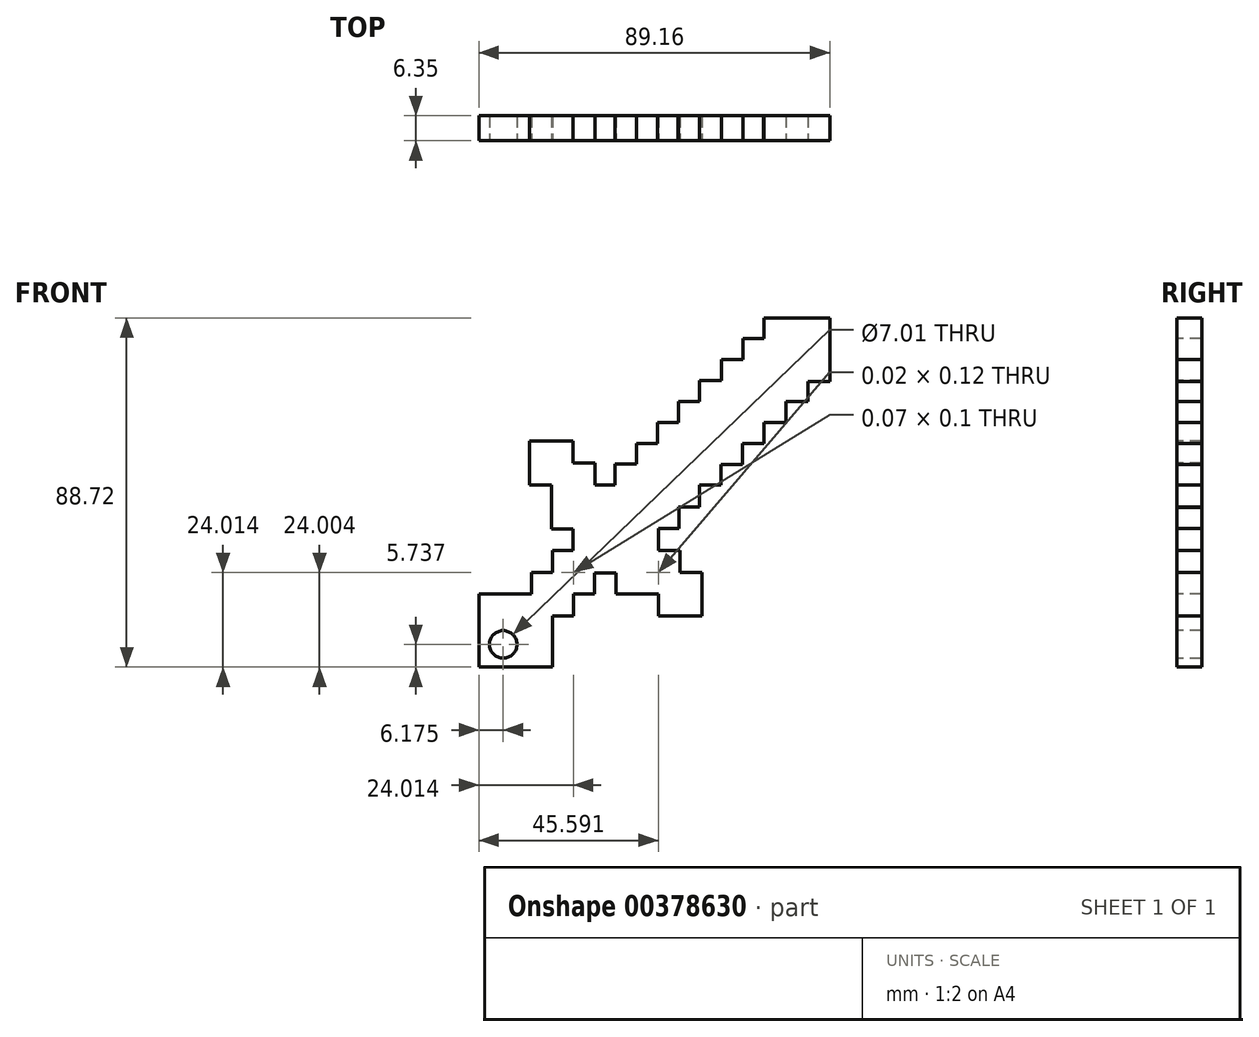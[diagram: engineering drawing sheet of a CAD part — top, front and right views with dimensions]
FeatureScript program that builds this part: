
annotation { "Feature Type Name" : "Feature", "Feature Type Description" : "" }
export const myFeature = defineFeature(function(context is Context, id is Id, definition is map)
    precondition{}
    {
        {
            var Q0;
            Q0=qCreatedBy(makeId("Front.planeOp"),FACE);
            var sketch = newSketch(context, id + "F0", { "sketchPlane" : qUnion([Q0])});
            skLineSegment(sketch, "E0.bottom", {"start": v(-54.91, -24.94) * mm, "end": v(-36.22, -24.94) * mm});
            skLineSegment(sketch, "E0.top", {"start": v(-54.91, -43.46) * mm, "end": v(-36.22, -43.46) * mm});
            skLineSegment(sketch, "E0.left", {"start": v(-54.91, -24.94) * mm, "end": v(-54.91, -43.46) * mm});
            skLineSegment(sketch, "E0.right", {"start": v(-36.22, -24.94) * mm, "end": v(-36.22, -43.46) * mm});
            skPoint(sketch, "E1", {"position": v(-45.57, -34.2) * mm});
            skPoint(sketch, "E2.orphan", {"position": v(-45.57, -24.94) * mm});
            skPoint(sketch, "E3.orphan", {"position": v(-36.22, -34.2) * mm});
            skPoint(sketch, "E4.end.orphan", {"position": v(-45.57, -43.46) * mm});
            skPoint(sketch, "E5.start.orphan", {"position": v(-54.91, -34.2) * mm});
            skLineSegment(sketch, "E6.bottom", {"start": v(-41.62, -37.8) * mm, "end": v(-49.52, -37.8) * mm});
            skLineSegment(sketch, "E6.top", {"start": v(-41.62, -30.6) * mm, "end": v(-49.52, -30.6) * mm});
            skLineSegment(sketch, "E6.left", {"start": v(-41.62, -37.8) * mm, "end": v(-41.62, -30.6) * mm});
            skLineSegment(sketch, "E6.right", {"start": v(-49.52, -37.8) * mm, "end": v(-49.52, -30.6) * mm});
            skLineSegment(sketch, "E7.bottom", {"start": v(-30.86, -19.4) * mm, "end": v(-41.59, -19.4) * mm});
            skLineSegment(sketch, "E7.top", {"start": v(-30.86, -30.48) * mm, "end": v(-41.59, -30.48) * mm});
            skLineSegment(sketch, "E7.left", {"start": v(-30.86, -19.4) * mm, "end": v(-30.86, -30.48) * mm});
            skLineSegment(sketch, "E7.right", {"start": v(-41.59, -19.4) * mm, "end": v(-41.59, -30.48) * mm});
            skPoint(sketch, "E7.middle", {"position": v(-36.22, -24.94) * mm});
            skLineSegment(sketch, "E8.bottom", {"start": v(-25.5, -24.94) * mm, "end": v(-36.22, -24.94) * mm});
            skLineSegment(sketch, "E8.top", {"start": v(-25.5, -13.87) * mm, "end": v(-36.22, -13.87) * mm});
            skLineSegment(sketch, "E8.left", {"start": v(-25.5, -24.94) * mm, "end": v(-25.5, -13.87) * mm});
            skLineSegment(sketch, "E8.right", {"start": v(-36.22, -24.94) * mm, "end": v(-36.22, -13.87) * mm});
            skPoint(sketch, "E8.middle", {"position": v(-30.86, -19.4) * mm});
            skLineSegment(sketch, "E9.bottom", {"start": v(-20.13, -8.39) * mm, "end": v(-30.93, -8.39) * mm});
            skLineSegment(sketch, "E9.left", {"start": v(-20.13, -8.39) * mm, "end": v(-20.13, -19.35) * mm});
            skPoint(sketch, "E9.middle", {"position": v(-25.5, -13.87) * mm});
            skLineSegment(sketch, "E10.bottom", {"start": v(-14.86, -13.87) * mm, "end": v(-25.5, -13.87) * mm});
            skLineSegment(sketch, "E10.top", {"start": v(-14.86, -2.91) * mm, "end": v(-20.23, -2.91) * mm});
            skLineSegment(sketch, "E10.left", {"start": v(-14.86, -8.39) * mm, "end": v(-14.86, -2.91) * mm});
            skLineSegment(sketch, "E10.right", {"start": v(-25.4, -13.87) * mm, "end": v(-25.4, -2.91) * mm});
            skPoint(sketch, "E10.middle", {"position": v(-20.13, -8.39) * mm});
            skLineSegment(sketch, "E11.bottom", {"start": v(-9.5, -8.39) * mm, "end": v(-20.23, -8.39) * mm});
            skLineSegment(sketch, "E11.right", {"start": v(-20.23, -8.39) * mm, "end": v(-20.23, 2.73) * mm});
            skPoint(sketch, "E11.middle", {"position": v(-14.86, -2.91) * mm});
            skPoint(sketch, "E11.cornerSnap0", {"position": v(-14.86, -8.39) * mm});
            skPoint(sketch, "E12.middle", {"position": v(-9.5, 2.57) * mm});
            skLineSegment(sketch, "E13.bottom", {"start": v(-4.16, -2.9) * mm, "end": v(-14.84, -2.9) * mm});
            skLineSegment(sketch, "E13.top", {"start": v(-4.16, 8.04) * mm, "end": v(-14.84, 8.04) * mm});
            skLineSegment(sketch, "E13.left", {"start": v(-4.16, -2.9) * mm, "end": v(-4.16, 8.04) * mm});
            skLineSegment(sketch, "E13.right", {"start": v(-14.84, -2.9) * mm, "end": v(-14.84, 8.04) * mm});
            skLineSegment(sketch, "E14.bottom", {"start": v(1.16, 2.73) * mm, "end": v(-9.49, 2.73) * mm});
            skLineSegment(sketch, "E14.top", {"start": v(1.16, 13.36) * mm, "end": v(-9.49, 13.36) * mm});
            skLineSegment(sketch, "E14.left", {"start": v(1.16, 2.73) * mm, "end": v(1.16, 13.36) * mm});
            skLineSegment(sketch, "E14.right", {"start": v(-9.49, 2.73) * mm, "end": v(-9.49, 13.36) * mm});
            skPoint(sketch, "E14.middle", {"position": v(-4.16, 8.04) * mm});
            skLineSegment(sketch, "E15.bottom", {"start": v(6.6, 8.04) * mm, "end": v(-4.28, 8.04) * mm});
            skLineSegment(sketch, "E15.top", {"start": v(6.6, 18.68) * mm, "end": v(-4.28, 18.68) * mm});
            skLineSegment(sketch, "E15.left", {"start": v(6.6, 8.04) * mm, "end": v(6.6, 18.68) * mm});
            skLineSegment(sketch, "E15.right", {"start": v(-4.28, 8.04) * mm, "end": v(-4.28, 18.68) * mm});
            skPoint(sketch, "E15.middle", {"position": v(1.16, 13.36) * mm});
            skPoint(sketch, "E15.cornerSnap0", {"position": v(1.16, 8.04) * mm});
            skLineSegment(sketch, "E16.bottom", {"start": v(12.14, 13.36) * mm, "end": v(1.06, 13.36) * mm});
            skLineSegment(sketch, "E16.top", {"start": v(12.14, 24) * mm, "end": v(1.06, 24) * mm});
            skLineSegment(sketch, "E16.left", {"start": v(12.14, 13.36) * mm, "end": v(12.14, 24) * mm});
            skLineSegment(sketch, "E16.right", {"start": v(1.06, 13.36) * mm, "end": v(1.06, 24) * mm});
            skPoint(sketch, "E16.middle", {"position": v(6.6, 18.68) * mm});
            skLineSegment(sketch, "E17.bottom", {"start": v(17.58, 18.68) * mm, "end": v(6.7, 18.68) * mm});
            skLineSegment(sketch, "E17.top", {"start": v(17.58, 29.3) * mm, "end": v(6.7, 29.3) * mm});
            skLineSegment(sketch, "E17.left", {"start": v(17.58, 18.68) * mm, "end": v(17.58, 29.3) * mm});
            skLineSegment(sketch, "E17.right", {"start": v(6.7, 18.68) * mm, "end": v(6.7, 29.3) * mm});
            skPoint(sketch, "E17.middle", {"position": v(12.14, 24) * mm});
            skLineSegment(sketch, "E18.bottom", {"start": v(23.03, 24) * mm, "end": v(12.14, 24) * mm});
            skLineSegment(sketch, "E18.top", {"start": v(23.03, 34.62) * mm, "end": v(12.14, 34.62) * mm});
            skLineSegment(sketch, "E18.left", {"start": v(23.03, 24) * mm, "end": v(23.03, 34.62) * mm});
            skLineSegment(sketch, "E18.right", {"start": v(12.14, 24) * mm, "end": v(12.14, 34.62) * mm});
            skPoint(sketch, "E18.middle", {"position": v(17.58, 29.3) * mm});
            skLineSegment(sketch, "E19.bottom", {"start": v(28.63, 29.3) * mm, "end": v(17.42, 29.3) * mm});
            skLineSegment(sketch, "E19.top", {"start": v(28.63, 39.94) * mm, "end": v(17.42, 39.94) * mm});
            skLineSegment(sketch, "E19.left", {"start": v(28.63, 29.3) * mm, "end": v(28.63, 39.94) * mm});
            skLineSegment(sketch, "E19.right", {"start": v(17.42, 29.3) * mm, "end": v(17.42, 39.94) * mm});
            skPoint(sketch, "E19.middle", {"position": v(23.03, 34.62) * mm});
            skLineSegment(sketch, "E20.bottom", {"start": v(28.63, 34.62) * mm, "end": v(23.04, 34.62) * mm});
            skLineSegment(sketch, "E20.top", {"start": v(34.23, 45.26) * mm, "end": v(23.04, 45.26) * mm});
            skLineSegment(sketch, "E20.left", {"start": v(34.23, 34.62) * mm, "end": v(34.23, 45.26) * mm});
            skLineSegment(sketch, "E20.right", {"start": v(23.04, 34.62) * mm, "end": v(23.04, 39.94) * mm});
            skPoint(sketch, "E20.middle", {"position": v(28.63, 39.94) * mm});
            skLineSegment(sketch, "E21.bottom", {"start": v(-30.93, 2.73) * mm, "end": v(-9.33, 2.73) * mm});
            skLineSegment(sketch, "E21.top", {"start": v(-30.93, -19.5) * mm, "end": v(-9.33, -19.5) * mm});
            skLineSegment(sketch, "E21.left", {"start": v(-30.93, 2.73) * mm, "end": v(-30.93, -19.5) * mm});
            skLineSegment(sketch, "E21.right", {"start": v(-9.33, 2.73) * mm, "end": v(-9.33, -19.5) * mm});
            skLineSegment(sketch, "E22", {"start": v(-25.4, -2.91) * mm, "end": v(-25.4, 2.73) * mm});
            skLineSegment(sketch, "E23", {"start": v(-14.86, -13.87) * mm, "end": v(-9.33, -13.87) * mm});
            skLineSegment(sketch, "E24.MirrorCS", {"start": v(-36.47, -2.91) * mm, "end": v(-36.47, 2.73) * mm});
            skLineSegment(sketch, "E25.MirrorCS", {"start": v(-30.93, 2.73) * mm, "end": v(-36.47, 2.73) * mm});
            skLineSegment(sketch, "E26.MirrorCS", {"start": v(-36.47, -8.39) * mm, "end": v(-30.93, -8.39) * mm});
            skLineSegment(sketch, "E27.MirrorCS", {"start": v(-36.47, -8.39) * mm, "end": v(-36.47, -2.91) * mm});
            skPoint(sketch, "E28.orphan", {"position": v(-36.47, -13.87) * mm});
            skPoint(sketch, "E29.orphan", {"position": v(-41.73, -8.39) * mm});
            skPoint(sketch, "E30.orphan", {"position": v(-52.54, 2.73) * mm});
            skLineSegment(sketch, "E31.top", {"start": v(-25.4, 8.37) * mm, "end": v(-36.47, 8.37) * mm});
            skLineSegment(sketch, "E31.left", {"start": v(-25.4, -2.91) * mm, "end": v(-25.4, 8.37) * mm});
            skLineSegment(sketch, "E31.right", {"start": v(-36.47, -2.91) * mm, "end": v(-36.47, 8.37) * mm});
            skPoint(sketch, "E31.middle", {"position": v(-30.93, 2.73) * mm});
            skLineSegment(sketch, "E32.bottom", {"start": v(-30.93, 2.73) * mm, "end": v(-42, 2.73) * mm});
            skLineSegment(sketch, "E32.top", {"start": v(-30.93, 14) * mm, "end": v(-42, 14) * mm});
            skLineSegment(sketch, "E32.left", {"start": v(-30.93, 2.73) * mm, "end": v(-30.93, 14) * mm});
            skLineSegment(sketch, "E32.right", {"start": v(-42, 2.73) * mm, "end": v(-42, 14) * mm});
            skPoint(sketch, "E32.middle", {"position": v(-36.47, 8.37) * mm});
            skPoint(sketch, "E33.orphan", {"position": v(-31, -8.39) * mm});
            skPoint(sketch, "E34.orphan", {"position": v(-30.86, -8.39) * mm});
            skPoint(sketch, "E35.orphan", {"position": v(-30.86, -19.35) * mm});
            skLineSegment(sketch, "E36.bottom", {"start": v(-14.84, -24.85) * mm, "end": v(-20.13, -24.85) * mm});
            skLineSegment(sketch, "E36.left", {"start": v(-14.84, -19.5) * mm, "end": v(-14.84, -13.85) * mm});
            skPoint(sketch, "E36.middle", {"position": v(-20.13, -19.35) * mm});
            skLineSegment(sketch, "E37", {"start": v(-20.13, -19.35) * mm, "end": v(-20.13, -24.85) * mm});
            skLineSegment(sketch, "E38.bottom", {"start": v(-14.84, -19.5) * mm, "end": v(-9.3, -19.5) * mm});
            skLineSegment(sketch, "E38.top", {"start": v(-14.84, -24.92) * mm, "end": v(-9.3, -24.92) * mm});
            skLineSegment(sketch, "E38.left", {"start": v(-14.84, -24.85) * mm, "end": v(-14.84, -24.92) * mm});
            skLineSegment(sketch, "E38.right", {"start": v(-9.3, -19.5) * mm, "end": v(-9.3, -24.92) * mm});
            skLineSegment(sketch, "E39.bottom", {"start": v(-9.33, -13.87) * mm, "end": v(-3.78, -13.87) * mm});
            skLineSegment(sketch, "E39.top", {"start": v(-9.33, -19.39) * mm, "end": v(-3.78, -19.39) * mm});
            skLineSegment(sketch, "E39.left", {"start": v(-9.33, -13.87) * mm, "end": v(-9.33, -19.39) * mm});
            skLineSegment(sketch, "E39.right", {"start": v(-3.78, -13.87) * mm, "end": v(-3.78, -19.39) * mm});
            skLineSegment(sketch, "E40.bottom", {"start": v(-3.78, -19.39) * mm, "end": v(-9.3, -19.39) * mm});
            skLineSegment(sketch, "E40.top", {"start": v(-3.78, -24.92) * mm, "end": v(-9.3, -24.92) * mm});
            skLineSegment(sketch, "E40.left", {"start": v(-3.78, -19.39) * mm, "end": v(-3.78, -24.92) * mm});
            skLineSegment(sketch, "E40.right", {"start": v(-9.3, -19.39) * mm, "end": v(-9.3, -24.92) * mm});
            skPoint(sketch, "E41.orphan", {"position": v(0, -13.87) * mm});
            skLineSegment(sketch, "E42.bottom", {"start": v(1.76, -30.45) * mm, "end": v(-9.3, -30.45) * mm});
            skLineSegment(sketch, "E42.top", {"start": v(1.76, -19.39) * mm, "end": v(-9.3, -19.39) * mm});
            skLineSegment(sketch, "E42.left", {"start": v(1.76, -30.45) * mm, "end": v(1.76, -19.39) * mm});
            skLineSegment(sketch, "E42.right", {"start": v(-9.3, -30.45) * mm, "end": v(-9.3, -19.39) * mm});
            skPoint(sketch, "E42.middle", {"position": v(-3.78, -24.92) * mm});
            skLineSegment(sketch, "E43.bottom", {"start": v(-9.5, 8.04) * mm, "end": v(-14.92, 8.04) * mm});
            skLineSegment(sketch, "E43.top", {"start": v(-9.49, 13.36) * mm, "end": v(-14.92, 13.36) * mm});
            skLineSegment(sketch, "E43.right", {"start": v(-14.92, 8.04) * mm, "end": v(-14.92, 13.36) * mm});
            skPoint(sketch, "E44.firstSnap0", {"position": v(-14.84, 2.57) * mm});
            skLineSegment(sketch, "E44.bottom", {"start": v(-14.84, 2.73) * mm, "end": v(-20.27, 2.73) * mm});
            skLineSegment(sketch, "E44.top", {"start": v(-14.84, 8.07) * mm, "end": v(-20.27, 8.07) * mm});
            skLineSegment(sketch, "E44.left", {"start": v(-14.84, 2.73) * mm, "end": v(-14.84, 8.07) * mm});
            skLineSegment(sketch, "E44.right", {"start": v(-20.27, 2.73) * mm, "end": v(-20.27, 8.07) * mm});
            skLineSegment(sketch, "E45.bottom", {"start": v(-4.16, 13.36) * mm, "end": v(-9.49, 13.36) * mm});
            skLineSegment(sketch, "E45.top", {"start": v(-4.16, 18.64) * mm, "end": v(-9.49, 18.64) * mm});
            skLineSegment(sketch, "E45.right", {"start": v(-9.49, 13.36) * mm, "end": v(-9.49, 18.64) * mm});
            skLineSegment(sketch, "E46.bottom", {"start": v(1.16, 18.68) * mm, "end": v(-4.2, 18.68) * mm});
            skLineSegment(sketch, "E46.top", {"start": v(1.16, 24) * mm, "end": v(-4.2, 24) * mm});
            skLineSegment(sketch, "E46.left", {"start": v(1.16, 24) * mm, "end": v(1.16, 24) * mm});
            skLineSegment(sketch, "E46.right", {"start": v(-4.2, 18.68) * mm, "end": v(-4.2, 24) * mm});
            skLineSegment(sketch, "E47.bottom", {"start": v(-9.33, -2.9) * mm, "end": v(-4.05, -2.9) * mm});
            skLineSegment(sketch, "E47.top", {"start": v(-9.33, -8.3) * mm, "end": v(-4.05, -8.3) * mm});
            skLineSegment(sketch, "E47.left", {"start": v(-9.33, -2.9) * mm, "end": v(-9.33, -8.3) * mm});
            skLineSegment(sketch, "E47.right", {"start": v(-4.05, -2.9) * mm, "end": v(-4.05, -8.3) * mm});
            skLineSegment(sketch, "E48.bottom", {"start": v(-4.16, 2.73) * mm, "end": v(1.13, 2.73) * mm});
            skLineSegment(sketch, "E48.top", {"start": v(-4.16, -2.74) * mm, "end": v(1.13, -2.74) * mm});
            skLineSegment(sketch, "E48.left", {"start": v(-4.16, 2.73) * mm, "end": v(-4.16, -2.74) * mm});
            skLineSegment(sketch, "E48.right", {"start": v(1.13, 2.73) * mm, "end": v(1.13, -2.74) * mm});
            skLineSegment(sketch, "E49.bottom", {"start": v(1.16, 8.04) * mm, "end": v(6.61, 8.04) * mm});
            skLineSegment(sketch, "E49.top", {"start": v(1.16, 2.74) * mm, "end": v(6.61, 2.74) * mm});
            skLineSegment(sketch, "E49.left", {"start": v(1.16, 8.04) * mm, "end": v(1.16, 2.74) * mm});
            skLineSegment(sketch, "E49.right", {"start": v(6.61, 8.04) * mm, "end": v(6.61, 2.74) * mm});
            skLineSegment(sketch, "E50.bottom", {"start": v(6.7, 24) * mm, "end": v(1.16, 24) * mm});
            skLineSegment(sketch, "E50.top", {"start": v(6.7, 29.28) * mm, "end": v(1.16, 29.28) * mm});
            skLineSegment(sketch, "E50.left", {"start": v(6.7, 24) * mm, "end": v(6.7, 29.28) * mm});
            skLineSegment(sketch, "E50.right", {"start": v(1.16, 24) * mm, "end": v(1.16, 29.28) * mm});
            skLineSegment(sketch, "E51.bottom", {"start": v(12.14, 29.3) * mm, "end": v(6.7, 29.3) * mm});
            skLineSegment(sketch, "E51.top", {"start": v(12.14, 34.67) * mm, "end": v(6.7, 34.67) * mm});
            skLineSegment(sketch, "E51.left", {"start": v(12.14, 29.3) * mm, "end": v(12.14, 34.67) * mm});
            skLineSegment(sketch, "E51.right", {"start": v(6.7, 29.3) * mm, "end": v(6.7, 34.67) * mm});
            skPoint(sketch, "E52.firstSnap0", {"position": v(6.6, 13.36) * mm});
            skLineSegment(sketch, "E52.bottom", {"start": v(6.7, 13.36) * mm, "end": v(12.06, 13.36) * mm});
            skLineSegment(sketch, "E52.top", {"start": v(6.61, 8.04) * mm, "end": v(12.06, 8.04) * mm});
            skLineSegment(sketch, "E52.right", {"start": v(12.06, 13.36) * mm, "end": v(12.06, 8.04) * mm});
            skLineSegment(sketch, "E53.bottom", {"start": v(12.14, 18.68) * mm, "end": v(17.58, 18.68) * mm});
            skLineSegment(sketch, "E53.top", {"start": v(12.14, 13.39) * mm, "end": v(17.58, 13.39) * mm});
            skLineSegment(sketch, "E53.left", {"start": v(12.14, 18.68) * mm, "end": v(12.14, 13.39) * mm});
            skLineSegment(sketch, "E53.right", {"start": v(17.58, 18.68) * mm, "end": v(17.58, 13.39) * mm});
            skLineSegment(sketch, "E54.bottom", {"start": v(17.58, 24) * mm, "end": v(23.15, 24) * mm});
            skLineSegment(sketch, "E54.top", {"start": v(17.58, 18.68) * mm, "end": v(23.15, 18.68) * mm});
            skLineSegment(sketch, "E54.left", {"start": v(17.58, 24) * mm, "end": v(17.58, 18.68) * mm});
            skLineSegment(sketch, "E54.right", {"start": v(23.15, 24) * mm, "end": v(23.15, 18.68) * mm});
            skLineSegment(sketch, "E55.bottom", {"start": v(23.03, 29.3) * mm, "end": v(28.65, 29.3) * mm});
            skLineSegment(sketch, "E55.top", {"start": v(23.03, 23.98) * mm, "end": v(28.65, 23.98) * mm});
            skLineSegment(sketch, "E55.left", {"start": v(23.03, 29.3) * mm, "end": v(23.03, 23.98) * mm});
            skLineSegment(sketch, "E55.right", {"start": v(28.65, 29.3) * mm, "end": v(28.65, 23.98) * mm});
            skLineSegment(sketch, "E56.bottom", {"start": v(34.23, 34.62) * mm, "end": v(34.25, 34.62) * mm});
            skLineSegment(sketch, "E56.top", {"start": v(28.63, 29.08) * mm, "end": v(34.25, 29.08) * mm});
            skLineSegment(sketch, "E56.left", {"start": v(28.63, 34.62) * mm, "end": v(28.63, 29.08) * mm});
            skLineSegment(sketch, "E56.right", {"start": v(34.25, 34.62) * mm, "end": v(34.25, 29.08) * mm});
            skLineSegment(sketch, "E57.bottom", {"start": v(17.42, 34.62) * mm, "end": v(12.14, 34.62) * mm});
            skLineSegment(sketch, "E57.top", {"start": v(17.42, 39.97) * mm, "end": v(12.14, 39.97) * mm});
            skLineSegment(sketch, "E57.left", {"start": v(17.42, 34.62) * mm, "end": v(17.42, 39.97) * mm});
            skLineSegment(sketch, "E57.right", {"start": v(12.14, 34.62) * mm, "end": v(12.14, 39.97) * mm});
            skLineSegment(sketch, "E58.bottom", {"start": v(23.04, 39.94) * mm, "end": v(17.58, 39.94) * mm});
            skLineSegment(sketch, "E58.top", {"start": v(23.04, 45.26) * mm, "end": v(17.58, 45.26) * mm});
            skLineSegment(sketch, "E58.right", {"start": v(17.58, 39.94) * mm, "end": v(17.58, 45.26) * mm});
            skLineSegment(sketch, "E59.bottom", {"start": v(28.63, 39.94) * mm, "end": v(34.23, 39.94) * mm});
            skLineSegment(sketch, "E59.top", {"start": v(28.63, 45.26) * mm, "end": v(34.23, 45.26) * mm});
            skLineSegment(sketch, "E59.left", {"start": v(28.63, 39.94) * mm, "end": v(28.63, 45.26) * mm});
            skLineSegment(sketch, "E59.right", {"start": v(34.23, 39.94) * mm, "end": v(34.23, 45.26) * mm});
            skPoint(sketch, "E60.orphan", {"position": v(-25.42, -24.85) * mm});
            skPoint(sketch, "E61.trimOffspring.end.orphan", {"position": v(-25.42, -13.85) * mm});
            skPoint(sketch, "E62.orphan", {"position": v(-20.23, 2.57) * mm});
            skSolve(sketch);
        }
        {
            var Q0;
            {var subQ1=sQuery(id+"F0.wireOp",EDGE,"E16.top");var subQ3=sQuery(id+"F0.wireOp",EDGE,"E15.top");var subQ6=sQuery(id+"F0.wireOp",EDGE,"E46.left");var subQ12=makeQuery(id+"F0.imprint","IMPRINT",EDGE,{"derivedFrom":subQ6});var subQ13=sQuery(id+"F0.wireOp",EDGE,"E37");var subQ14=sQuery(id+"F0.wireOp",EDGE,"E36.bottom");var subQ15=sQuery(id+"F0.wireOp",EDGE,"E21.top");var subQ17=sQuery(id+"F0.wireOp",EDGE,"E36.left");var subQ18=makeQuery(id+"F0.imprint","INTERSECT",VERTEX,{"derivedFrom":[subQ15,subQ17]});var subQ24=makeQuery(id+"F0.imprint","IMPRINT",EDGE,{"derivedFrom":sQuery(id+"F0.wireOp",EDGE,"E38.right")});var subQ25=sQuery(id+"F0.wireOp",EDGE,"E49.bottom");var subQ26=makeQuery(id+"F0.imprint","IMPRINT",EDGE,{"derivedFrom":subQ25});var subQ37=sQuery(id+"F0.wireOp",EDGE,"E14.bottom");var subQ39=sQuery(id+"F0.wireOp",EDGE,"E13.left");var subQ43=sQuery(id+"F0.wireOp",EDGE,"E47.bottom");var subQ46=sQuery(id+"F0.wireOp",EDGE,"E48.top");var subQ47=makeQuery(id+"F0.imprint","INTERSECT",VERTEX,{"derivedFrom":[subQ39,subQ46]});var subQ48=makeQuery(id+"F0.imprint","IMPRINT",EDGE,{"disambiguationData":[TD([[subQ47,-1.0]])],"derivedFrom":subQ39});var subQ50=sQuery(id+"F0.wireOp",EDGE,"E17.right");var subQ58=makeQuery(id+"F0.imprint","INTERSECT",VERTEX,{"derivedFrom":[subQ1,subQ50]});var subQ59=makeQuery(id+"F0.imprint","IMPRINT",EDGE,{"disambiguationData":[TD([[subQ58,-1.0]])],"derivedFrom":subQ50});var subQ61=sQuery(id+"F0.wireOp",EDGE,"E16.left");var subQ72=makeQuery(id+"F0.imprint","IMPRINT",EDGE,{"derivedFrom":sQuery(id+"F0.wireOp",EDGE,"E40.top")});var subQ73=sQuery(id+"F0.wireOp",EDGE,"E15.right");var subQ74=sQuery(id+"F0.wireOp",EDGE,"E13.top");var subQ75=makeQuery(id+"F0.imprint","INTERSECT",VERTEX,{"derivedFrom":[subQ74,subQ73]});var subQ78=sQuery(id+"F0.wireOp",EDGE,"E45.right");var subQ79=sQuery(id+"F0.wireOp",EDGE,"E43.top");var subQ80=sQuery(id+"F0.wireOp",EDGE,"E14.top");var subQ91=sQuery(id+"F0.wireOp",EDGE,"E21.left");var subQ92=sQuery(id+"F0.wireOp",EDGE,"E7.bottom");var subQ93=makeQuery(id+"F0.imprint","INTERSECT",VERTEX,{"derivedFrom":[subQ92,subQ91]});var subQ97=sQuery(id+"F0.wireOp",EDGE,"E7.left");var subQ102=sQuery(id+"F0.wireOp",EDGE,"E39.bottom");var subQ106=sQuery(id+"F0.wireOp",EDGE,"E51.left");var subQ107=makeQuery(id+"F0.imprint","IMPRINT",EDGE,{"derivedFrom":subQ106});var subQ115=sQuery(id+"F0.wireOp",EDGE,"E48.right");var subQ116=makeQuery(id+"F0.imprint","INTERSECT",VERTEX,{"derivedFrom":[subQ37,subQ115]});var subQ119=makeQuery(id+"F0.imprint","IMPRINT",EDGE,{"disambiguationData":[TD([[subQ116,-1.0]])],"derivedFrom":subQ37});var subQ121=sQuery(id+"F0.wireOp",EDGE,"E54.top");var subQ125=sQuery(id+"F0.wireOp",EDGE,"E54.bottom");var subQ131=sQuery(id+"F0.wireOp",EDGE,"E17.bottom");var subQ136=sQuery(id+"F0.wireOp",EDGE,"E43.bottom");var subQ137=makeQuery(id+"F0.imprint","IMPRINT",EDGE,{"derivedFrom":subQ136});var subQ153=sQuery(id+"F0.wireOp",EDGE,"E9.bottom");var subQ155=sQuery(id+"F0.wireOp",EDGE,"E10.top");var subQ158=sQuery(id+"F0.wireOp",EDGE,"E10.right");var subQ159=makeQuery(id+"F0.imprint","INTERSECT",VERTEX,{"derivedFrom":[subQ153,subQ158]});var subQ160=sQuery(id+"F0.wireOp",EDGE,"E22");var subQ162=sQuery(id+"F0.wireOp",EDGE,"E31.left");var subQ164=makeQuery(id+"F0.imprint","IMPRINT",EDGE,{"derivedFrom":subQ160});var subQ172=makeQuery(id+"F0.imprint","IMPRINT",VERTEX,{"derivedFrom":subQ80});var subQ177=makeQuery(id+"F0.imprint","INTERSECT",VERTEX,{"derivedFrom":[subQ61,subQ131]});var subQ178=sQuery(id+"F0.wireOp",EDGE,"E53.top");var subQ185=sQuery(id+"F0.wireOp",EDGE,"E8.bottom");var subQ186=makeQuery(id+"F0.imprint","INTERSECT",VERTEX,{"derivedFrom":[subQ97,subQ185]});var subQ187=makeQuery(id+"F0.imprint","IMPRINT",EDGE,{"disambiguationData":[TD([[subQ186,1.0]])],"derivedFrom":subQ97});var subQ189=sQuery(id+"F0.wireOp",EDGE,"E8.right");var subQ190=makeQuery(id+"F0.imprint","INTERSECT",VERTEX,{"derivedFrom":[subQ92,subQ189]});var subQ191=makeQuery(id+"F0.imprint","IMPRINT",EDGE,{"disambiguationData":[TD([[subQ190,1.0]])],"derivedFrom":subQ92});var subQ193=sQuery(id+"F0.wireOp",EDGE,"E0.right");var subQ194=sQuery(id+"F0.wireOp",EDGE,"E0.bottom");var subQ195=makeQuery(id+"F0.imprint","INTERSECT",VERTEX,{"derivedFrom":[subQ194,subQ193]});var subQ198=makeQuery(id+"F0.imprint","IMPRINT",EDGE,{"disambiguationData":[TD([[subQ195,1.0]])],"derivedFrom":subQ194});var subQ210=sQuery(id+"F0.wireOp",EDGE,"E0.top");var subQ213=sQuery(id+"F0.wireOp",EDGE,"E31.right");var subQ214=makeQuery(id+"F0.imprint","IMPRINT",EDGE,{"derivedFrom":subQ213});var subQ219=sQuery(id+"F0.wireOp",EDGE,"E25.MirrorCS");var subQ220=makeQuery(id+"F0.imprint","IMPRINT",EDGE,{"derivedFrom":subQ219});var subQ225=makeQuery(id+"F0.imprint","IMPRINT",VERTEX,{"derivedFrom":subQ3});var subQ234=sQuery(id+"F0.wireOp",EDGE,"E55.bottom");var subQ241=sQuery(id+"F0.wireOp",EDGE,"E20.bottom");var subQ257=sQuery(id+"F0.wireOp",EDGE,"E9.left");var subQ268=sQuery(id+"F0.wireOp",EDGE,"E59.bottom");var subQ270=makeQuery(id+"F0.imprint","IMPRINT",EDGE,{"derivedFrom":subQ268});var subQ272=makeQuery(id+"F0.imprint","IMPRINT",EDGE,{"derivedFrom":subQ125});var subQ274=makeQuery(id+"F0.imprint","INTERSECT",VERTEX,{"derivedFrom":[subQ257,subQ13]});var subQ275=makeQuery(id+"F0.imprint","IMPRINT",EDGE,{"disambiguationData":[TD([[subQ274,1.0]])],"derivedFrom":subQ257});var subQ277=makeQuery(id+"F0.imprint","IMPRINT",EDGE,{"derivedFrom":subQ234});var subQ285=sQuery(id+"F0.wireOp",EDGE,"E58.top");var subQ288=makeQuery(id+"F0.imprint","IMPRINT",EDGE,{"disambiguationData":[TD([[subQ18,-1.0]])],"derivedFrom":subQ17});Q0=qUnion([makeQuery(id+"F0.imprint","IMPRINT",FACE,{"disambiguationData":[TD([[subQ26,-1.0]])]}),makeQuery(id+"F0.imprint","IMPRINT",FACE,{"disambiguationData":[TD([[makeQuery(id+"F0.imprint","IMPRINT",EDGE,{"derivedFrom":subQ79}),1.0]])]}),makeQuery(id+"F0.imprint","IMPRINT",FACE,{"disambiguationData":[TD([[subQ277,1.0]])]}),makeQuery(id+"F0.imprint","IMPRINT",FACE,{"disambiguationData":[TD([[subQ275,1.0]])]}),makeQuery(id+"F0.imprint","IMPRINT",FACE,{"disambiguationData":[TD([[subQ288,-1.0]])]}),makeQuery(id+"F0.imprint","IMPRINT",FACE,{"disambiguationData":[TD([[subQ272,1.0]])]}),makeQuery(id+"F0.imprint","IMPRINT",FACE,{"disambiguationData":[TD([[makeQuery(id+"F0.imprint","IMPRINT",EDGE,{"derivedFrom":sQuery(id+"F0.wireOp",EDGE,"E24.MirrorCS")}),-1.0]])]}),makeQuery(id+"F0.imprint","IMPRINT",FACE,{"disambiguationData":[TD([[makeQuery(id+"F0.imprint","IMPRINT",EDGE,{"derivedFrom":subQ285}),1.0]])]}),makeQuery(id+"F0.imprint","IMPRINT",FACE,{"disambiguationData":[TD([[subQ164,1.0]])]}),makeQuery(id+"F0.imprint","IMPRINT",FACE,{"disambiguationData":[TD([[subQ277,-1.0]])]}),makeQuery(id+"F0.imprint","IMPRINT",FACE,{"disambiguationData":[TD([[subQ275,-1.0]])]}),makeQuery(id+"F0.imprint","IMPRINT",FACE,{"disambiguationData":[TD([[subQ272,-1.0]])]}),makeQuery(id+"F0.imprint","IMPRINT",FACE,{"disambiguationData":[TD([[subQ270,1.0]])]}),makeQuery(id+"F0.imprint","IMPRINT",FACE,{"disambiguationData":[TD([[makeQuery(id+"F0.imprint","IMPRINT",EDGE,{"derivedFrom":subQ155}),-1.0]])]}),makeQuery(id+"F0.imprint","IMPRINT",FACE,{"disambiguationData":[TD([[makeQuery(id+"F0.imprint","IMPRINT",EDGE,{"disambiguationData":[TD([[subQ159,1.0]])],"derivedFrom":subQ158}),1.0]])]}),makeQuery(id+"F0.imprint","IMPRINT",FACE,{"disambiguationData":[TD([[makeQuery(id+"F0.imprint","IMPRINT",EDGE,{"derivedFrom":subQ162}),1.0]])]}),makeQuery(id+"F0.imprint","IMPRINT",FACE,{"disambiguationData":[TD([[subQ137,-1.0]])]}),makeQuery(id+"F0.imprint","IMPRINT",FACE,{"disambiguationData":[TD([[makeQuery(id+"F0.imprint","IMPRINT",EDGE,{"derivedFrom":subQ241}),1.0]])]}),makeQuery(id+"F0.imprint","IMPRINT",FACE,{"disambiguationData":[TD([[subQ191,1.0]])]}),makeQuery(id+"F0.imprint","IMPRINT",FACE,{"disambiguationData":[TD([[makeQuery(id+"F0.imprint","IMPRINT",EDGE,{"disambiguationData":[TD([[subQ225,1.0]])],"derivedFrom":subQ3}),-1.0]])]}),makeQuery(id+"F0.imprint","IMPRINT",FACE,{"disambiguationData":[TD([[makeQuery(id+"F0.imprint","IMPRINT",EDGE,{"disambiguationData":[TD([[subQ177,-1.0]])],"derivedFrom":subQ61}),-1.0]])]}),makeQuery(id+"F0.imprint","IMPRINT",FACE,{"disambiguationData":[TD([[subQ220,-1.0]])]}),makeQuery(id+"F0.imprint","IMPRINT",FACE,{"disambiguationData":[TD([[subQ214,1.0]])]}),makeQuery(id+"F0.imprint","IMPRINT",FACE,{"disambiguationData":[TD([[subQ72,1.0]])]}),makeQuery(id+"F0.imprint","IMPRINT",FACE,{"disambiguationData":[TD([[makeQuery(id+"F0.imprint","IMPRINT",EDGE,{"derivedFrom":subQ210}),1.0]])]}),makeQuery(id+"F0.imprint","IMPRINT",FACE,{"disambiguationData":[TD([[subQ198,1.0]])]}),makeQuery(id+"F0.imprint","IMPRINT",FACE,{"disambiguationData":[TD([[subQ198,-1.0]])]}),makeQuery(id+"F0.imprint","IMPRINT",FACE,{"disambiguationData":[TD([[subQ191,-1.0]])]}),makeQuery(id+"F0.imprint","IMPRINT",FACE,{"disambiguationData":[TD([[subQ187,1.0]])]}),makeQuery(id+"F0.imprint","IMPRINT",FACE,{"disambiguationData":[TD([[makeQuery(id+"F0.imprint","IMPRINT",EDGE,{"derivedFrom":subQ43}),-1.0]])]}),makeQuery(id+"F0.imprint","IMPRINT",FACE,{"disambiguationData":[TD([[makeQuery(id+"F0.imprint","IMPRINT",EDGE,{"derivedFrom":subQ46}),1.0]])]}),makeQuery(id+"F0.imprint","IMPRINT",FACE,{"disambiguationData":[TD([[makeQuery(id+"F0.imprint","IMPRINT",EDGE,{"derivedFrom":subQ78}),-1.0]])]}),makeQuery(id+"F0.imprint","IMPRINT",FACE,{"disambiguationData":[TD([[makeQuery(id+"F0.imprint","IMPRINT",EDGE,{"derivedFrom":subQ178}),1.0]])]}),makeQuery(id+"F0.imprint","IMPRINT",FACE,{"disambiguationData":[TD([[makeQuery(id+"F0.imprint","IMPRINT",EDGE,{"disambiguationData":[TD([[subQ172,1.0]])],"derivedFrom":subQ80}),-1.0]])]}),makeQuery(id+"F0.imprint","IMPRINT",FACE,{"disambiguationData":[TD([[subQ107,-1.0]])]}),makeQuery(id+"F0.imprint","IMPRINT",FACE,{"disambiguationData":[TD([[subQ164,-1.0]])]}),makeQuery(id+"F0.imprint","IMPRINT",FACE,{"disambiguationData":[TD([[subQ137,1.0]])]}),makeQuery(id+"F0.imprint","IMPRINT",FACE,{"disambiguationData":[TD([[makeQuery(id+"F0.imprint","IMPRINT",EDGE,{"derivedFrom":subQ121}),1.0]])]}),makeQuery(id+"F0.imprint","IMPRINT",FACE,{"disambiguationData":[TD([[subQ119,-1.0]])]}),makeQuery(id+"F0.imprint","IMPRINT",FACE,{"disambiguationData":[TD([[makeQuery(id+"F0.imprint","IMPRINT",EDGE,{"derivedFrom":sQuery(id+"F0.wireOp",EDGE,"E51.top")}),1.0]])]}),makeQuery(id+"F0.imprint","IMPRINT",FACE,{"disambiguationData":[TD([[makeQuery(id+"F0.imprint","IMPRINT",EDGE,{"derivedFrom":subQ102}),-1.0]])]}),makeQuery(id+"F0.imprint","IMPRINT",FACE,{"disambiguationData":[TD([[makeQuery(id+"F0.imprint","IMPRINT",EDGE,{"disambiguationData":[TD([[subQ93,1.0]])],"derivedFrom":subQ92}),-1.0]])]}),makeQuery(id+"F0.imprint","IMPRINT",FACE,{"disambiguationData":[TD([[makeQuery(id+"F0.imprint","IMPRINT",EDGE,{"disambiguationData":[TD([[subQ75,-1.0]])],"derivedFrom":subQ74}),-1.0]])]}),makeQuery(id+"F0.imprint","IMPRINT",FACE,{"disambiguationData":[TD([[subQ24,1.0]])]}),makeQuery(id+"F0.imprint","IMPRINT",FACE,{"disambiguationData":[TD([[subQ12,-1.0]])]}),makeQuery(id+"F0.imprint","IMPRINT",FACE,{"disambiguationData":[TD([[subQ59,-1.0]])]}),makeQuery(id+"F0.imprint","IMPRINT",FACE,{"disambiguationData":[TD([[subQ48,1.0]])]}),makeQuery(id+"F0.imprint","IMPRINT",FACE,{"disambiguationData":[TD([[subQ26,1.0]])]}),makeQuery(id+"F0.imprint","IMPRINT",FACE,{"disambiguationData":[TD([[makeQuery(id+"F0.imprint","IMPRINT",EDGE,{"derivedFrom":subQ14}),-1.0]])]}),makeQuery(id+"F0.imprint","IMPRINT",FACE,{"disambiguationData":[TD([[makeQuery(id+"F0.imprint","IMPRINT",EDGE,{"derivedFrom":sQuery(id+"F0.wireOp",EDGE,"E46.top")}),1.0]])]})]);}
            var Q1;
            {var subQ6=sQuery(id+"F0.wireOp",EDGE,"E9.left");var subQ8=sQuery(id+"F0.wireOp",EDGE,"E37");var subQ9=makeQuery(id+"F0.imprint","INTERSECT",VERTEX,{"derivedFrom":[subQ6,subQ8]});Q1=makeQuery(id+"F0.imprint","IMPRINT",FACE,{"disambiguationData":[TD([[makeQuery(id+"F0.imprint","IMPRINT",EDGE,{"disambiguationData":[TD([[subQ9,1.0]])],"derivedFrom":subQ6}),-1.0]])]});}
            var Q2;
            {var subQ3=sQuery(id+"F0.wireOp",EDGE,"E10.right");var subQ5=sQuery(id+"F0.wireOp",EDGE,"E9.bottom");var subQ8=makeQuery(id+"F0.imprint","INTERSECT",VERTEX,{"derivedFrom":[subQ5,subQ3]});Q2=makeQuery(id+"F0.imprint","IMPRINT",FACE,{"disambiguationData":[TD([[makeQuery(id+"F0.imprint","IMPRINT",EDGE,{"disambiguationData":[TD([[subQ8,1.0]])],"derivedFrom":subQ5}),1.0]])]});}
            var Q3;
            Q3=makeQuery(id+"F0.imprint","IMPRINT",FACE,{"disambiguationData":[TD([[makeQuery(id+"F0.imprint","IMPRINT",EDGE,{"derivedFrom":sQuery(id+"F0.wireOp",EDGE,"E6.bottom")}),-1.0]])]});
            var Q4;
            {var subQ14=sQuery(id+"F0.wireOp",EDGE,"E10.top");Q4=makeQuery(id+"F0.imprint","IMPRINT",FACE,{"disambiguationData":[TD([[makeQuery(id+"F0.imprint","IMPRINT",EDGE,{"derivedFrom":subQ14}),-1.0]])]});}
            var Q5;
            {var subQ1=sQuery(id+"F0.wireOp",EDGE,"E10.top");Q5=makeQuery(id+"F0.imprint","IMPRINT",FACE,{"disambiguationData":[TD([[makeQuery(id+"F0.imprint","IMPRINT",EDGE,{"derivedFrom":subQ1}),1.0]])]});}
            var Q6;
            {var subQ0=sQuery(id+"F0.wireOp",EDGE,"E11.left");var subQ1=sQuery(id+"F0.wireOp",EDGE,"E11.top");var subQ2=makeQuery(id+"F0.imprint","INTERSECT",VERTEX,{"derivedFrom":[subQ1,subQ0]});Q6=makeQuery(id+"F0.imprint","IMPRINT",FACE,{"disambiguationData":[TD([[makeQuery(id+"F0.imprint","IMPRINT",EDGE,{"disambiguationData":[TD([[subQ2,-1.0]])],"derivedFrom":subQ1}),1.0]])]});}
            var Q7;
            {var subQ0=sQuery(id+"F0.wireOp",EDGE,"E14.top");var subQ4=makeQuery(id+"F0.imprint","IMPRINT",VERTEX,{"derivedFrom":subQ0});Q7=makeQuery(id+"F0.imprint","IMPRINT",FACE,{"disambiguationData":[TD([[makeQuery(id+"F0.imprint","IMPRINT",EDGE,{"disambiguationData":[TD([[subQ4,1.0]])],"derivedFrom":subQ0}),1.0]])]});}
            var Q8;
            {var subQ3=sQuery(id+"F0.wireOp",EDGE,"E16.left");var subQ5=sQuery(id+"F0.wireOp",EDGE,"E17.bottom");var subQ6=makeQuery(id+"F0.imprint","INTERSECT",VERTEX,{"derivedFrom":[subQ3,subQ5]});Q8=makeQuery(id+"F0.imprint","IMPRINT",FACE,{"disambiguationData":[TD([[makeQuery(id+"F0.imprint","IMPRINT",EDGE,{"disambiguationData":[TD([[subQ6,-1.0]])],"derivedFrom":subQ5}),-1.0]])]});}
            var Q9;
            {var subQ0=sQuery(id+"F0.wireOp",EDGE,"E18.right");var subQ5=sQuery(id+"F0.wireOp",EDGE,"E17.top");var subQ7=makeQuery(id+"F0.imprint","INTERSECT",VERTEX,{"derivedFrom":[subQ5,subQ0]});Q9=makeQuery(id+"F0.imprint","IMPRINT",FACE,{"disambiguationData":[TD([[makeQuery(id+"F0.imprint","IMPRINT",EDGE,{"disambiguationData":[TD([[subQ7,1.0]])],"derivedFrom":subQ5}),1.0]])]});}
            var Q10;
            {var subQ0=sQuery(id+"F0.wireOp",EDGE,"E18.right");var subQ1=sQuery(id+"F0.wireOp",EDGE,"E17.top");var subQ2=makeQuery(id+"F0.imprint","INTERSECT",VERTEX,{"derivedFrom":[subQ1,subQ0]});Q10=makeQuery(id+"F0.imprint","IMPRINT",FACE,{"disambiguationData":[TD([[makeQuery(id+"F0.imprint","IMPRINT",EDGE,{"disambiguationData":[TD([[subQ2,1.0]])],"derivedFrom":subQ1}),-1.0]])]});}
            var Q11;
            {var subQ0=sQuery(id+"F0.wireOp",EDGE,"E18.left");var subQ1=sQuery(id+"F0.wireOp",EDGE,"E18.top");var subQ2=makeQuery(id+"F0.imprint","INTERSECT",VERTEX,{"derivedFrom":[subQ1,subQ0]});Q11=makeQuery(id+"F0.imprint","IMPRINT",FACE,{"disambiguationData":[TD([[makeQuery(id+"F0.imprint","IMPRINT",EDGE,{"disambiguationData":[TD([[subQ2,-1.0]])],"derivedFrom":subQ1}),1.0]])]});}
            var Q12;
            {var subQ1=sQuery(id+"F0.wireOp",EDGE,"E17.left");var subQ3=sQuery(id+"F0.wireOp",EDGE,"E18.bottom");var subQ4=makeQuery(id+"F0.imprint","INTERSECT",VERTEX,{"derivedFrom":[subQ1,subQ3]});Q12=makeQuery(id+"F0.imprint","IMPRINT",FACE,{"disambiguationData":[TD([[makeQuery(id+"F0.imprint","IMPRINT",EDGE,{"disambiguationData":[TD([[subQ4,-1.0]])],"derivedFrom":subQ1}),-1.0]])]});}
            var Q13;
            {var subQ4=sQuery(id+"F0.wireOp",EDGE,"E20.bottom");Q13=makeQuery(id+"F0.imprint","IMPRINT",FACE,{"disambiguationData":[TD([[makeQuery(id+"F0.imprint","IMPRINT",EDGE,{"derivedFrom":subQ4}),-1.0]])]});}
            var Q14;
            {var subQ5=sQuery(id+"F0.wireOp",EDGE,"E21.right");var subQ7=sQuery(id+"F0.wireOp",EDGE,"E13.bottom");var subQ9=makeQuery(id+"F0.imprint","INTERSECT",VERTEX,{"derivedFrom":[subQ7,subQ5]});Q14=makeQuery(id+"F0.imprint","IMPRINT",FACE,{"disambiguationData":[TD([[makeQuery(id+"F0.imprint","IMPRINT",EDGE,{"disambiguationData":[TD([[subQ9,-1.0]])],"derivedFrom":subQ7}),-1.0]])]});}
            var Q15;
            {var subQ1=sQuery(id+"F0.wireOp",EDGE,"E13.top");var subQ5=makeQuery(id+"F0.imprint","IMPRINT",VERTEX,{"derivedFrom":subQ1});Q15=makeQuery(id+"F0.imprint","IMPRINT",FACE,{"disambiguationData":[TD([[makeQuery(id+"F0.imprint","IMPRINT",EDGE,{"disambiguationData":[TD([[subQ5,1.0]])],"derivedFrom":subQ1}),1.0]])]});}
            var Q16;
            {var subQ4=sQuery(id+"F0.wireOp",EDGE,"E13.top");var subQ6=makeQuery(id+"F0.imprint","INTERSECT",VERTEX,{"derivedFrom":[subQ4,sQuery(id+"F0.wireOp",EDGE,"E15.right")]});Q16=makeQuery(id+"F0.imprint","IMPRINT",FACE,{"disambiguationData":[TD([[makeQuery(id+"F0.imprint","IMPRINT",EDGE,{"disambiguationData":[TD([[subQ6,-1.0]])],"derivedFrom":subQ4}),1.0]])]});}
            var Q17;
            {var subQ1=sQuery(id+"F0.wireOp",EDGE,"E15.top");var subQ5=makeQuery(id+"F0.imprint","IMPRINT",VERTEX,{"derivedFrom":subQ1});Q17=makeQuery(id+"F0.imprint","IMPRINT",FACE,{"disambiguationData":[TD([[makeQuery(id+"F0.imprint","IMPRINT",EDGE,{"disambiguationData":[TD([[subQ5,1.0]])],"derivedFrom":subQ1}),1.0]])]});}
            var Q18;
            {var subQ0=sQuery(id+"F0.wireOp",EDGE,"E15.bottom");var subQ1=sQuery(id+"F0.wireOp",EDGE,"E14.left");var subQ2=makeQuery(id+"F0.imprint","INTERSECT",VERTEX,{"derivedFrom":[subQ1,subQ0]});Q18=makeQuery(id+"F0.imprint","IMPRINT",FACE,{"disambiguationData":[TD([[makeQuery(id+"F0.imprint","IMPRINT",EDGE,{"disambiguationData":[TD([[subQ2,-1.0]])],"derivedFrom":subQ1}),-1.0]])]});}
            extrude(context, id + "F1", {"entities" : qUnion([Q0, Q1, Q2, Q3, Q4, Q5, Q6, Q7, Q8, Q9, Q10, Q11, Q12, Q13, Q14, Q15, Q16, Q17, Q18]), "oppositeDirection" : true, "depth" : 6.35 * mm});
        }
        {
            var Q0;
            Q0=qCreatedBy(makeId("Front.planeOp"),FACE);
            var sketch = newSketch(context, id + "F2", { "sketchPlane" : qUnion([Q0])});
            skCircle(sketch, "E63", {"center": v(-48.73, -37.72) * mm, "radius": 3.5 * mm});
            skSolve(sketch);
        }
        {
            var Q0;
            Q0 = qSketchRegion(id + "F2", true);
            extrude(context, id + "F3", {"entities" : qUnion([Q0]), "operationType" : NewBodyOperationType.REMOVE, "oppositeDirection" : true, "depth" : 6.35 * mm, "offsetDistance" : 25.4 * mm});
        }
    });
